# Revit family: Broan®-FRESH_IN™-Motorized_Supply_Damper
name_source: partatom
category: Mechanical Equipment
units: mm (PartAtom-declared; Revit-internal decimal feet)

## family parameters
Always vertical = No
Classification = None
Cut with Voids When Loaded = No
Part Type = Normal
Room Calculation Point = No
Round Connector Dimension = Use Diameter
Shared = No
Work Plane-Based = Yes

## types (1)
- FIN-6MD
    Air Volume = 0 CFM
    Default Elevation = 0.00"
    Exhaust Air Connection Diameter = 6"
    Fan Wattage = 0 W
    Frequency = 60 Hz
    Height = 7.75"
    Length = 6.38"
    Manufacturer = Broan
    Model = FIN-6MD
    Noise = 0
    Number of Poles = 1
    Operating Weight = 2.50 lb
    Phase = 1
    Power Factor = 0
    Product Documentation Link = https://www.broan-nutone.com
    Product Name = Broan® FRESH IN™ Motorized Supply Damper
    Product Page URL = https://www.broan-nutone.com
    Requirements and Standards = ASHRAE 62.2
UL 1995
    URL = https://www.broan-nutone.com
    Voltage = 24 V
    Width = 10.63"
    c Lenght = 3.26"
    c MC width = 3.13"
    c Offset vent side = 1.35"
    c Vent Height = 2.15"
    c Width = 22.00"

## geometry (parser evidence)
native form markers: Sweep x6
no freeform markers — native parametric forms only
